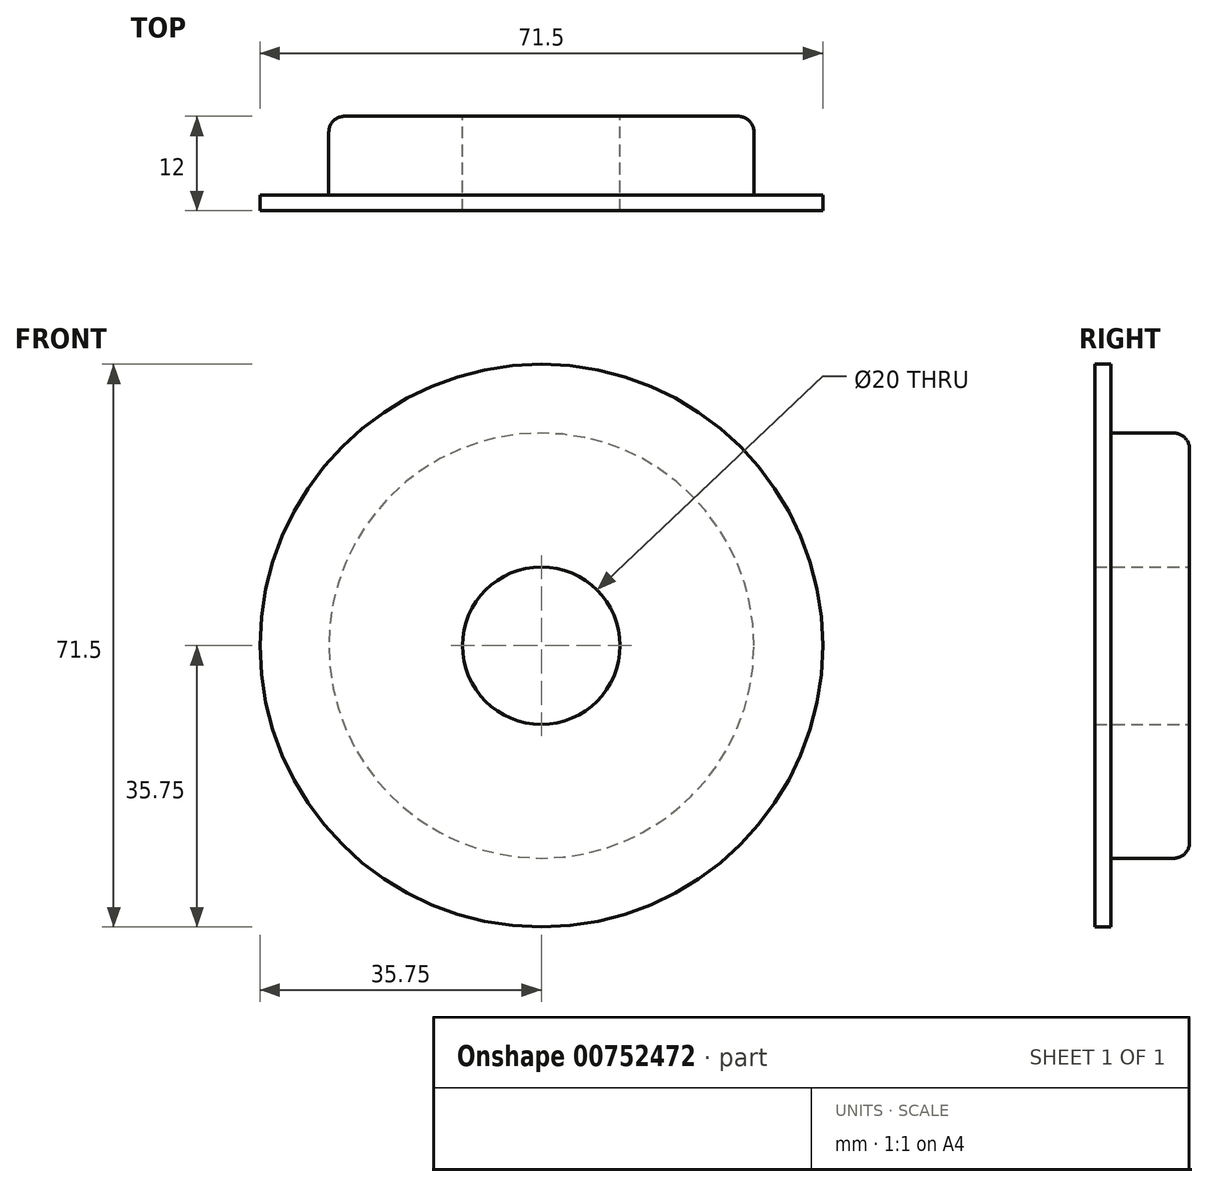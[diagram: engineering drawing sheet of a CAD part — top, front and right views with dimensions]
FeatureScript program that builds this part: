
annotation { "Feature Type Name" : "Feature", "Feature Type Description" : "" }
export const myFeature = defineFeature(function(context is Context, id is Id, definition is map)
    precondition{}
    {
        {
            var Q0;
            Q0=qCreatedBy(makeId("Front.planeOp"),FACE);
            var sketch = newSketch(context, id + "F0", { "sketchPlane" : qUnion([Q0])});
            skCircle(sketch, "E0", {"center": v(0, 0) * mm, "radius": 35.75 * mm});
            skCircle(sketch, "E1", {"center": v(0, 0) * mm, "radius": 10 * mm});
            skSolve(sketch);
        }
        {
            var Q0;
            Q0=makeQuery(id+"F0.imprint","IMPRINT",FACE,{"disambiguationData":[TD([[makeQuery(id+"F0.imprint","IMPRINT",EDGE,{"derivedFrom":sQuery(id+"F0.wireOp",EDGE,"E0")}),1.0]])]});
            extrude(context, id + "F1", {"entities" : qUnion([Q0]), "depth" : 2 * mm, "offsetDistance" : 25 * mm});
        }
        {
            var Q0;
            Q0=makeQuery(id+"F1.opExtrude","CAP_FACE",FACE,{"disambiguationData":[OSD([sQuery(id+"F0.wireOp",EDGE,"E0"),sQuery(id+"F0.wireOp",EDGE,"E1")])],"isStart":true});
            var sketch = newSketch(context, id + "F2", { "sketchPlane" : qUnion([Q0])});
            skCircle(sketch, "E2", {"center": v(0, 0) * mm, "radius": 27 * mm});
            skSolve(sketch);
        }
        {
            var Q0;
            Q0=makeQuery(id+"F2.imprint","IMPRINT",FACE,{"disambiguationData":[TD([[makeQuery(id+"F2.imprint","IMPRINT",EDGE,{"derivedFrom":sQuery(id+"F2.wireOp",EDGE,"E2")}),1.0]])]});
            extrude(context, id + "F3", {"entities" : qUnion([Q0]), "operationType" : NewBodyOperationType.ADD, "depth" : 10 * mm, "offsetDistance" : 25 * mm});
        }
        {
            var Q0;
            Q0=makeQuery(id+"F3.opExtrude","CAP_EDGE",EDGE,{"disambiguationData":[OSD([sQuery(id+"F2.wireOp",EDGE,"E2")])],"isStart":false});
            fillet(context, id + "F4", {"entities" : qUnion([Q0]), "radius" : 2 * mm, "tangentPropagation" : true, "allowEdgeOverflow" : false});
        }
    });
